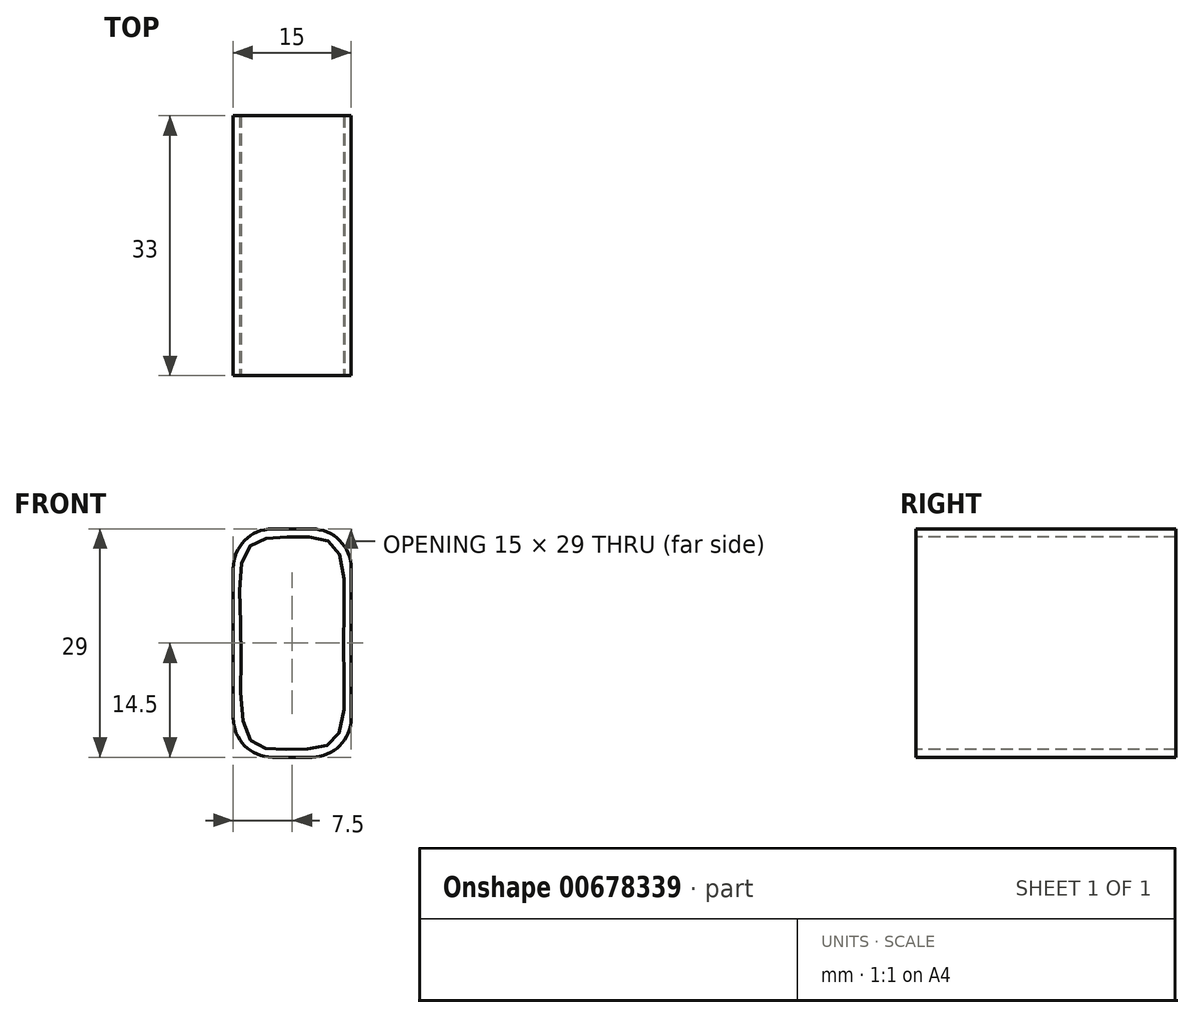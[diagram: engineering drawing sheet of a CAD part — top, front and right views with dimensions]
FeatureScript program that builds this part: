
annotation { "Feature Type Name" : "Feature", "Feature Type Description" : "" }
export const myFeature = defineFeature(function(context is Context, id is Id, definition is map)
    precondition{}
    {
        {
            var Q0;
            Q0=qCreatedBy(makeId("Top.planeOp"),FACE);
            var sketch = newSketch(context, id + "F0", { "sketchPlane" : qUnion([Q0])});
            skLineSegment(sketch, "E0.bottom", {"start": v(27.38, 15.88) * mm, "end": v(42.38, 15.88) * mm});
            skLineSegment(sketch, "E0.top", {"start": v(27.38, -17.12) * mm, "end": v(42.38, -17.12) * mm});
            skLineSegment(sketch, "E0.left", {"start": v(27.38, 15.88) * mm, "end": v(27.38, -17.12) * mm});
            skLineSegment(sketch, "E0.right", {"start": v(42.38, 15.88) * mm, "end": v(42.38, -17.12) * mm});
            skSolve(sketch);
        }
        {
            var Q0;
            Q0=makeQuery(id+"F0.imprint","IMPRINT",FACE,{"disambiguationData":[TD([[makeQuery(id+"F0.imprint","IMPRINT",EDGE,{"derivedFrom":sQuery(id+"F0.wireOp",EDGE,"E0.bottom")}),-1.0]])]});
            extrude(context, id + "F1", {"entities" : qUnion([Q0]), "depth" : 29 * mm, "offsetDistance" : 25 * mm});
        }
        {
            var Q0;
            Q0 = qSketchRegion(id + "F0", true);
            extrude(context, id + "F2", {"entities" : qUnion([Q0]), "operationType" : NewBodyOperationType.ADD, "depth" : 10 * mm, "offsetDistance" : 25 * mm});
        }
        {
            var Q0;
            Q0=makeQuery(id+"F1.opExtrude","CAP_EDGE",EDGE,{"disambiguationData":[OSD([sQuery(id+"F0.wireOp",EDGE,"E0.right")])],"isStart":true});
            var Q1;
            Q1=makeQuery(id+"F1.opExtrude","CAP_EDGE",EDGE,{"disambiguationData":[OSD([sQuery(id+"F0.wireOp",EDGE,"E0.right")])],"isStart":false});
            var Q2;
            Q2=makeQuery(id+"F1.opExtrude","CAP_EDGE",EDGE,{"disambiguationData":[OSD([sQuery(id+"F0.wireOp",EDGE,"E0.left")])],"isStart":false});
            var Q3;
            Q3=makeQuery(id+"F1.opExtrude","CAP_EDGE",EDGE,{"disambiguationData":[OSD([sQuery(id+"F0.wireOp",EDGE,"E0.left")])],"isStart":true});
            fillet(context, id + "F3", {"entities" : qUnion([Q0, Q1, Q2, Q3]), "radius" : 5 * mm, "tangentPropagation" : true, "allowEdgeOverflow" : false});
        }
        {
            var Q0;
            Q0=makeQuery(id+"F1.opExtrude","SWEPT_FACE",FACE,{"disambiguationData":[OSD([sQuery(id+"F0.wireOp",EDGE,"E0.bottom")])]});
            var sketch = newSketch(context, id + "F4", { "sketchPlane" : qUnion([Q0])});
            skPoint(sketch, "E1", {"position": v(-41.38, 14.3) * mm});
            skPoint(sketch, "E2", {"position": v(-28.38, 14.78) * mm});
            skPoint(sketch, "E3", {"position": v(-34.83, 28) * mm});
            skPoint(sketch, "E4", {"position": v(-34.86, 1) * mm});
            skPoint(sketch, "E5", {"position": v(-40.36, 2.3) * mm});
            skPoint(sketch, "E6", {"position": v(-29.33, 26.66) * mm});
            skPoint(sketch, "E7", {"position": v(-40.36, 26.7) * mm});
            skPoint(sketch, "E8", {"position": v(-29.6, 2.12) * mm});
            skFitSpline(sketch, "E9", {"points": [v(-41.38, 14.3) * mm, v(-40.36, 2.3) * mm, v(-34.86, 1) * mm, v(-29.6, 2.12) * mm, v(-28.38, 14.78) * mm, v(-29.33, 26.66) * mm, v(-34.83, 28) * mm, v(-40.36, 26.7) * mm, v(-41.38, 14.3) * mm]});
            skSolve(sketch);
        }
        {
            var Q0;
            Q0=makeQuery(id+"F4.imprint","IMPRINT",FACE,{"disambiguationData":[TD([[makeQuery(id+"F4.imprint","IMPRINT",EDGE,{"derivedFrom":sQuery(id+"F4.wireOp",EDGE,"E9")}),1.0]])]});
            extrude(context, id + "F5", {"entities" : qUnion([Q0]), "operationType" : NewBodyOperationType.REMOVE, "oppositeDirection" : true, "depth" : 36 * mm, "offsetDistance" : 25 * mm});
        }
    });
